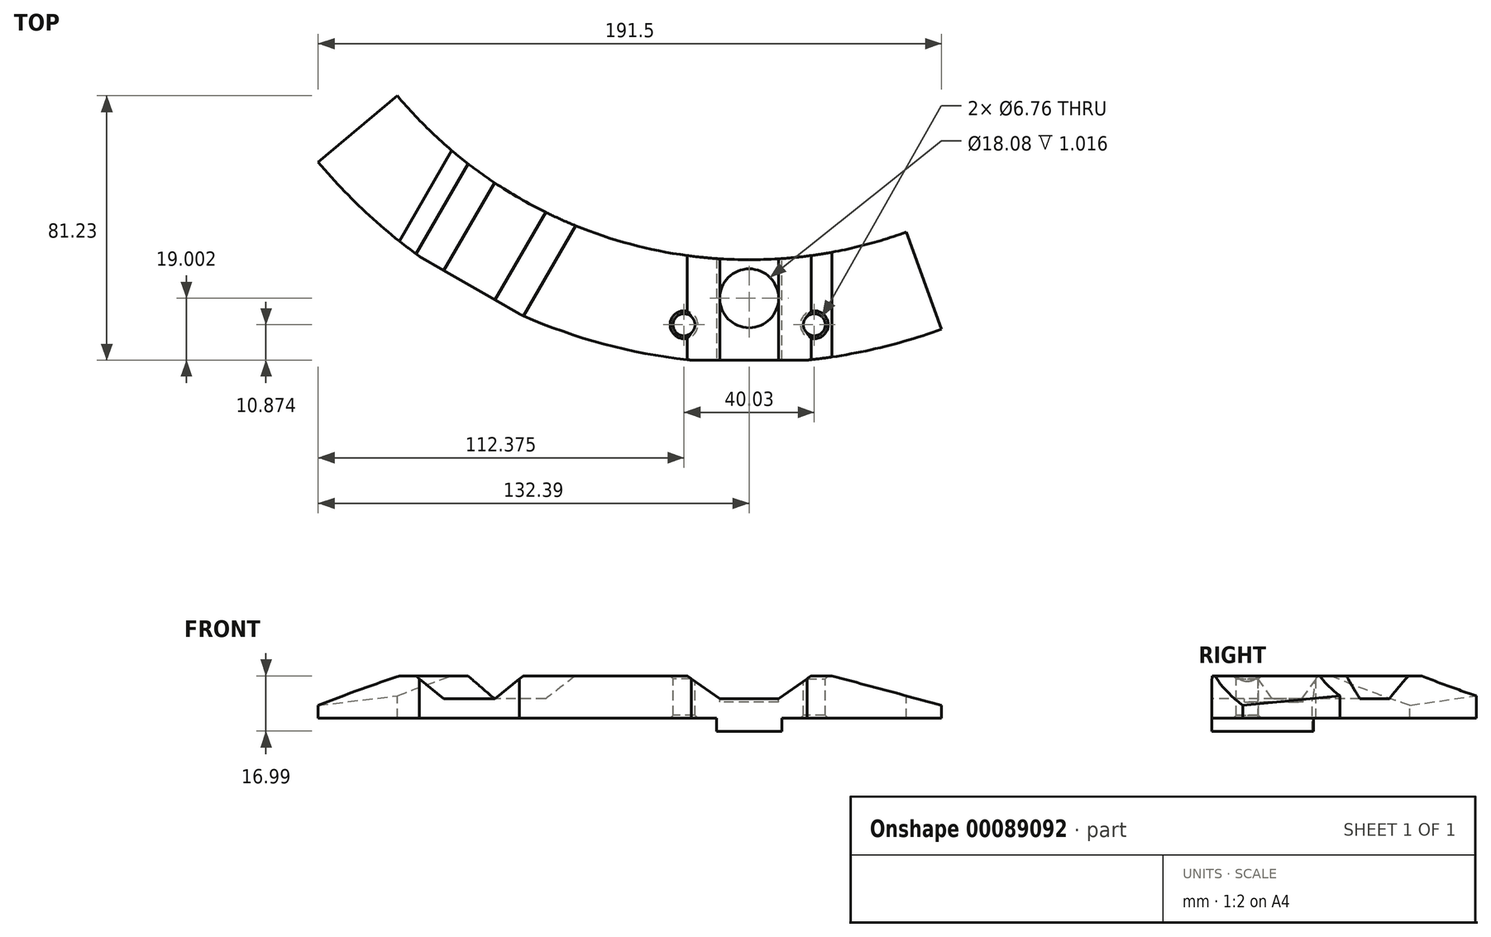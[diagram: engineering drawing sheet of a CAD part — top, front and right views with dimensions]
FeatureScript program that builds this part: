
annotation { "Feature Type Name" : "Feature", "Feature Type Description" : "" }
export const myFeature = defineFeature(function(context is Context, id is Id, definition is map)
    precondition{}
    {
        {
            var Q0;
            Q0=qCreatedBy(makeId("Top.planeOp"),FACE);
            var sketch = newSketch(context, id + "F0", { "sketchPlane" : qUnion([Q0])});
            skArc(sketch, "E0", {"start": v(-108.07, -90.68) * mm, "mid": v(-36.51, -136.26) * mm, "end": v(48.25, -132.56) * mm});
            skArc(sketch, "E1", {"start": v(-132.39, -111.09) * mm, "mid": v(-44.73, -166.93) * mm, "end": v(59.1, -162.4) * mm});
            skCircle(sketch, "E2", {"center": v(0, -152.9) * mm, "radius": 9.04 * mm});
            skCircle(sketch, "E3", {"center": v(-20.02, -161.04) * mm, "radius": 3.38 * mm});
            skCircle(sketch, "E4", {"center": v(20.02, -161.04) * mm, "radius": 3.38 * mm});
            skLineSegment(sketch, "E5", {"start": v(48.25, -132.56) * mm, "end": v(59.1, -162.4) * mm});
            skLineSegment(sketch, "E6", {"start": v(-108.07, -90.68) * mm, "end": v(-132.39, -111.09) * mm});
            skLineSegment(sketch, "E7", {"start": v(0, 0) * mm, "end": v(0, -200.83) * mm, "construction": true});
            skCircle(sketch, "E8", {"center": v(0, -152.9) * mm, "radius": 10 * mm});
            skSolve(sketch);
        }
        {
            var Q0;
            Q0=makeQuery(id+"F0.imprint","IMPRINT",FACE,{"disambiguationData":[TD([[makeQuery(id+"F0.imprint","IMPRINT",EDGE,{"derivedFrom":sQuery(id+"F0.wireOp",EDGE,"E0")}),-1.0]])]});
            var Q1;
            Q1=makeQuery(id+"F0.imprint","IMPRINT",FACE,{"disambiguationData":[TD([[makeQuery(id+"F0.imprint","IMPRINT",EDGE,{"derivedFrom":sQuery(id+"F0.wireOp",EDGE,"E2")}),1.0]])]});
            var Q2;
            Q2=makeQuery(id+"F0.imprint","IMPRINT",FACE,{"disambiguationData":[TD([[makeQuery(id+"F0.imprint","IMPRINT",EDGE,{"derivedFrom":sQuery(id+"F0.wireOp",EDGE,"E2")}),-1.0]])]});
            extrude(context, id + "F1", {"entities" : qUnion([Q0, Q1, Q2]), "oppositeDirection" : true, "depth" : 13 * mm});
        }
        {
            var Q0;
            Q0=makeQuery(id+"F0.imprint","IMPRINT",FACE,{"disambiguationData":[TD([[makeQuery(id+"F0.imprint","IMPRINT",EDGE,{"derivedFrom":sQuery(id+"F0.wireOp",EDGE,"E2")}),1.0]])]});
            extrude(context, id + "F2", {"entities" : qUnion([Q0]), "operationType" : NewBodyOperationType.REMOVE, "oppositeDirection" : true, "depth" : 8 * mm});
        }
        {
            var Q0;
            Q0=makeQuery(id+"F0.imprint","IMPRINT",FACE,{"disambiguationData":[TD([[makeQuery(id+"F0.imprint","IMPRINT",EDGE,{"derivedFrom":sQuery(id+"F0.wireOp",EDGE,"E2")}),-1.0]])]});
            extrude(context, id + "F3", {"entities" : qUnion([Q0]), "operationType" : NewBodyOperationType.REMOVE, "oppositeDirection" : true, "depth" : 1.52 * mm});
        }
        {
            var Q0;
            Q0=makeQuery(id+"F1.opExtrude","CAP_EDGE",EDGE,{"disambiguationData":[OSD([sQuery(id+"F0.wireOp",EDGE,"E3")])],"isStart":true});
            var Q1;
            Q1=makeQuery(id+"F1.opExtrude","CAP_EDGE",EDGE,{"disambiguationData":[OSD([sQuery(id+"F0.wireOp",EDGE,"E4")])],"isStart":true});
            var Q2;
            Q2=makeQuery(id+"F1.opExtrude","CAP_EDGE",EDGE,{"disambiguationData":[OSD([sQuery(id+"F0.wireOp",EDGE,"E3")])],"isStart":false});
            var Q3;
            Q3=makeQuery(id+"F1.opExtrude","CAP_EDGE",EDGE,{"disambiguationData":[OSD([sQuery(id+"F0.wireOp",EDGE,"E4")])],"isStart":false});
            chamfer(context, id + "F4", {"entities" : qUnion([Q0, Q1, Q2, Q3]), "width" : 0.89 * mm, "tangentPropagation" : true});
        }
        {
            var Q0;
            Q0=makeQuery(id+"F1.opExtrude","CAP_FACE",FACE,{"disambiguationData":[OSD([sQuery(id+"F0.wireOp",EDGE,"E0"),sQuery(id+"F0.wireOp",EDGE,"E1"),sQuery(id+"F0.wireOp",EDGE,"E3"),sQuery(id+"F0.wireOp",EDGE,"E4"),sQuery(id+"F0.wireOp",EDGE,"E5"),sQuery(id+"F0.wireOp",EDGE,"E6")])],"isStart":true});
            var sketch = newSketch(context, id + "F5", { "sketchPlane" : qUnion([Q0])});
            skLineSegment(sketch, "E9.bottom", {"start": v(-25.4, -176.99) * mm, "end": v(25.4, -176.99) * mm});
            skLineSegment(sketch, "E9.top", {"start": v(-25.4, -171.9) * mm, "end": v(25.4, -171.9) * mm});
            skLineSegment(sketch, "E9.left", {"start": v(-25.4, -176.99) * mm, "end": v(-25.4, -171.9) * mm});
            skLineSegment(sketch, "E9.right", {"start": v(25.4, -176.99) * mm, "end": v(25.4, -171.9) * mm});
            skLineSegment(sketch, "E10", {"start": v(-119.15, -129.7) * mm, "end": v(-58.66, -164.63) * mm});
            skLineSegment(sketch, "E11", {"start": v(-58.66, -164.63) * mm, "end": v(-61.2, -169.03) * mm});
            skLineSegment(sketch, "E12", {"start": v(-61.2, -169.03) * mm, "end": v(-121.7, -134.1) * mm});
            skLineSegment(sketch, "E13", {"start": v(-121.7, -134.1) * mm, "end": v(-119.15, -129.7) * mm});
            skSolve(sketch);
        }
        {
            var Q0;
            Q0 = qSketchRegion(id + "F5", true);
            extrude(context, id + "F6", {"entities" : qUnion([Q0]), "operationType" : NewBodyOperationType.REMOVE, "endBound" : BoundingType.THROUGH_ALL, "oppositeDirection" : true, "depth" : 25.4 * mm});
        }
        {
            var Q0;
            Q0=makeQuery(id+"F6.boolean.opBoolean","COPY",FACE,{"derivedFrom":makeQuery(id+"F6.opExtrude","SWEPT_FACE",FACE,{"disambiguationData":[OSD([sQuery(id+"F5.wireOp",EDGE,"E9.top")])]})});
            var sketch = newSketch(context, id + "F7", { "sketchPlane" : qUnion([Q0])});
            skLineSegment(sketch, "E14", {"start": v(-22.65, 2.54) * mm, "end": v(59.1, 2.54) * mm});
            skLineSegment(sketch, "E15", {"start": v(59.1, 2.54) * mm, "end": v(59.1, -9.03) * mm});
            skLineSegment(sketch, "E16", {"start": v(59.1, -9.03) * mm, "end": v(25.4, 0) * mm});
            skLineSegment(sketch, "E17", {"start": v(25.4, 0) * mm, "end": v(-25.4, 0) * mm});
            skLineSegment(sketch, "E18", {"start": v(25.4, 0) * mm, "end": v(19.02, 0) * mm});
            skLineSegment(sketch, "E19", {"start": v(19.02, 0) * mm, "end": v(9.04, -6.99) * mm});
            skLineSegment(sketch, "E20", {"start": v(9.04, -6.99) * mm, "end": v(-9.04, -6.99) * mm});
            skLineSegment(sketch, "E21", {"start": v(-9.04, -6.99) * mm, "end": v(-22.65, 2.54) * mm});
            skSolve(sketch);
        }
        {
            var Q0;
            Q0 = qSketchRegion(id + "F7", true);
            extrude(context, id + "F8", {"entities" : qUnion([Q0]), "operationType" : NewBodyOperationType.REMOVE, "endBound" : BoundingType.THROUGH_ALL, "oppositeDirection" : true, "depth" : 25.4 * mm});
        }
        {
            var Q0;
            Q0=makeQuery(id+"F1.opExtrude","CAP_FACE",FACE,{"disambiguationData":[OSD([sQuery(id+"F0.wireOp",EDGE,"E0"),sQuery(id+"F0.wireOp",EDGE,"E1"),sQuery(id+"F0.wireOp",EDGE,"E3"),sQuery(id+"F0.wireOp",EDGE,"E4"),sQuery(id+"F0.wireOp",EDGE,"E5"),sQuery(id+"F0.wireOp",EDGE,"E6")])],"isStart":false});
            var sketch = newSketch(context, id + "F9", { "sketchPlane" : qUnion([Q0])});
            skArc(sketch, "E22", {"start": v(10, 140.72) * mm, "mid": v(0, 141.07) * mm, "end": v(-10, 140.72) * mm});
            skLineSegment(sketch, "E23", {"start": v(-10, 140.72) * mm, "end": v(-10, 171.9) * mm});
            skLineSegment(sketch, "E24", {"start": v(-10, 171.9) * mm, "end": v(10, 171.9) * mm});
            skLineSegment(sketch, "E25", {"start": v(10, 171.9) * mm, "end": v(10, 140.72) * mm});
            skSolve(sketch);
        }
        {
            var Q0;
            Q0 = qSketchRegion(id + "F9", true);
            extrude(context, id + "F10", {"entities" : qUnion([Q0]), "operationType" : NewBodyOperationType.ADD, "depth" : 4 * mm});
        }
        {
            var Q0;
            Q0=makeQuery(id+"F6.boolean.opBoolean","COPY",FACE,{"derivedFrom":makeQuery(id+"F6.opExtrude","SWEPT_FACE",FACE,{"disambiguationData":[OSD([sQuery(id+"F5.wireOp",EDGE,"E10")])]})});
            var sketch = newSketch(context, id + "F11", { "sketchPlane" : qUnion([Q0])});
            skLineSegment(sketch, "E26", {"start": v(-19.02, 0) * mm, "end": v(-9.04, -6.99) * mm});
            skLineSegment(sketch, "E27", {"start": v(-9.04, -6.99) * mm, "end": v(9.12, -6.99) * mm});
            skLineSegment(sketch, "E28", {"start": v(9.12, -6.99) * mm, "end": v(19.1, 0) * mm});
            skLineSegment(sketch, "E29", {"start": v(19.1, 0) * mm, "end": v(-19.02, 0) * mm});
            skLineSegment(sketch, "E30", {"start": v(-25.4, 0) * mm, "end": v(-59.1, -9.03) * mm});
            skLineSegment(sketch, "E31", {"start": v(-59.1, -9.03) * mm, "end": v(-59.1, 0) * mm});
            skLineSegment(sketch, "E32", {"start": v(-59.1, 0) * mm, "end": v(-25.4, 0) * mm});
            skSolve(sketch);
        }
        {
            var Q0;
            Q0 = qSketchRegion(id + "F11", true);
            extrude(context, id + "F12", {"entities" : qUnion([Q0]), "operationType" : NewBodyOperationType.REMOVE, "endBound" : BoundingType.THROUGH_ALL, "oppositeDirection" : true, "depth" : 25.4 * mm});
        }
    });
